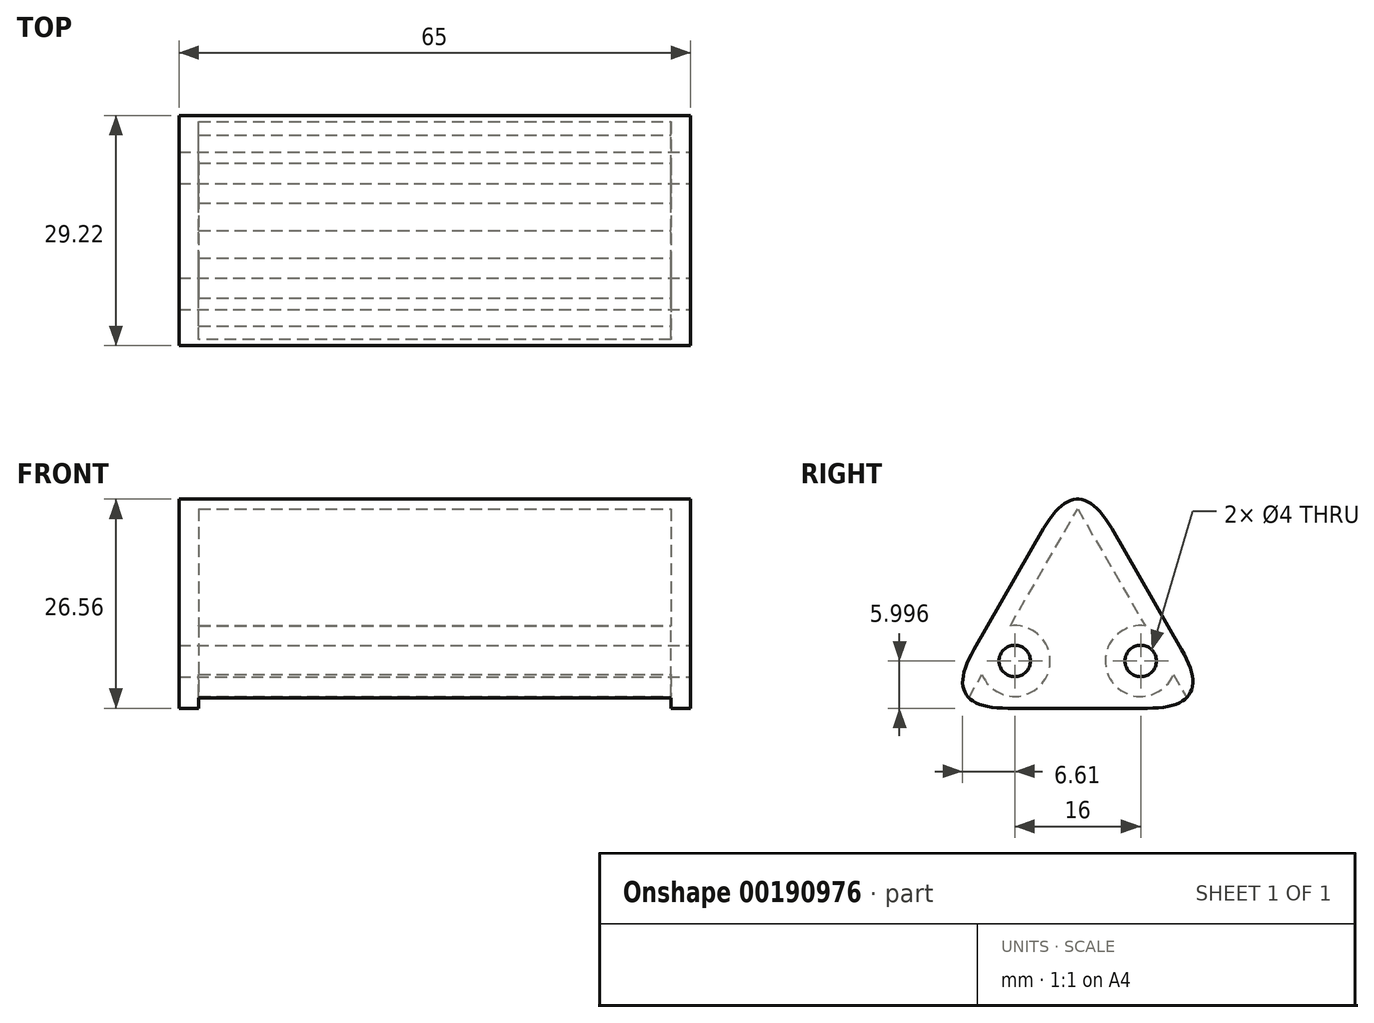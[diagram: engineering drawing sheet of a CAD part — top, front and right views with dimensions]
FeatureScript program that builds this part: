
annotation { "Feature Type Name" : "Feature", "Feature Type Description" : "" }
export const myFeature = defineFeature(function(context is Context, id is Id, definition is map)
    precondition{}
    {
        {
            var Q0;
            Q0=qCreatedBy(makeId("Right.planeOp"),FACE);
            var sketch = newSketch(context, id + "F0", { "sketchPlane" : qUnion([Q0])});
            skCircle(sketch, "E0.cCircle", {"center": v(0, 0) * mm, "radius": 10.1 * mm, "construction": true});
            skLineSegment(sketch, "E0.0", {"start": v(17.5, -10.1) * mm, "end": v(-17.5, -10.1) * mm});
            skLineSegment(sketch, "E0.1", {"start": v(-17.5, -10.1) * mm, "end": v(0, 20.2) * mm});
            skLineSegment(sketch, "E0.2", {"start": v(0, 20.2) * mm, "end": v(17.5, -10.1) * mm});
            skPoint(sketch, "E0.0.midPoint", {"position": v(0, -10.1) * mm});
            skLineSegment(sketch, "E1", {"start": v(-35.35, -17.57) * mm, "end": v(7.43, -17.57) * mm, "construction": true});
            skPoint(sketch, "E2", {"position": v(-8, -4.1) * mm});
            skLineSegment(sketch, "E3", {"start": v(0, 20.2) * mm, "end": v(0, -10.1) * mm, "construction": true});
            skPoint(sketch, "E4.MirrorP", {"position": v(8, -4.1) * mm});
            skSolve(sketch);
        }
        {
            var Q0;
            Q0=makeQuery(id+"F0.imprint","IMPRINT",FACE,{"disambiguationData":[TD([[makeQuery(id+"F0.imprint","IMPRINT",EDGE,{"derivedFrom":sQuery(id+"F0.wireOp",EDGE,"E0.0")}),-1.0]])]});
            extrude(context, id + "F1", {"entities" : qUnion([Q0]), "oppositeDirection" : true, "depth" : 65 * mm});
        }
        {
            var Q0;
            Q0=sQuery(id+"F0.wireOp",VERTEX,"E2");
            var Q1;
            Q1=sQuery(id+"F0.wireOp",VERTEX,"E4.MirrorP");
            var Q2;
            Q2=makeQuery(id+"F1.opExtrude","SWEPT_BODY",BODY,{"disambiguationData":[OSD([sQuery(id+"F0.wireOp",EDGE,"E0.0"),sQuery(id+"F0.wireOp",EDGE,"E0.1"),sQuery(id+"F0.wireOp",EDGE,"E0.2")])]});
            hole(context, id + "F2", {"style" : HoleStyle.SIMPLE, "endStyle" : HoleEndStyle.THROUGH, "holeDiameter" : 4 * mm, "locations" : qUnion([Q0, Q1]), "scope" : qUnion([Q2]), "isTappedThrough" : true});
        }
        {
            var Q0;
            Q0=makeQuery(id+"F1.opExtrude","SWEPT_FACE",FACE,{"disambiguationData":[OSD([sQuery(id+"F0.wireOp",EDGE,"E0.0")])]});
            var Q1;
            Q1=makeQuery(id+"F2.hole-0.boolean.opBoolean","COPY",FACE,{"derivedFrom":makeQuery(id+"F2.hole-0.opRevolve","SWEPT_FACE",FACE,{"disambiguationData":[OSD([sQuery(id+"F2.hole-0.sketch.wireOp",EDGE,"core_line_2")])]})});
            var Q2;
            Q2=makeQuery(id+"F2.hole-1.boolean.opBoolean","COPY",FACE,{"derivedFrom":makeQuery(id+"F2.hole-1.opRevolve","SWEPT_FACE",FACE,{"disambiguationData":[OSD([sQuery(id+"F2.hole-1.sketch.wireOp",EDGE,"core_line_2")])]})});
            shell(context, id + "F3", {"entities" : qUnion([Q0, Q1, Q2]), "thickness" : 2.5 * mm});
        }
        {
            var Q0;
            Q0=makeQuery(id+"F1.opExtrude","SWEPT_EDGE",EDGE,{"disambiguationData":[OSD([sQuery(id+"F0.wireOp",EDGE,"E0.1"),sQuery(id+"F0.wireOp",EDGE,"E0.2")])]});
            var Q1;
            Q1=makeQuery(id+"F1.opExtrude","SWEPT_EDGE",EDGE,{"disambiguationData":[OSD([sQuery(id+"F0.wireOp",EDGE,"E0.0"),sQuery(id+"F0.wireOp",EDGE,"E0.1")])]});
            var Q2;
            Q2=makeQuery(id+"F1.opExtrude","SWEPT_EDGE",EDGE,{"disambiguationData":[OSD([sQuery(id+"F0.wireOp",EDGE,"E0.0"),sQuery(id+"F0.wireOp",EDGE,"E0.2")])]});
            fillet(context, id + "F4", {"entities" : qUnion([Q0, Q1, Q2]), "radius" : 5 * mm, "tangentPropagation" : true, "rho" : 0.5, "crossSection" : FilletCrossSection.CONIC, "allowEdgeOverflow" : false});
        }
    });
